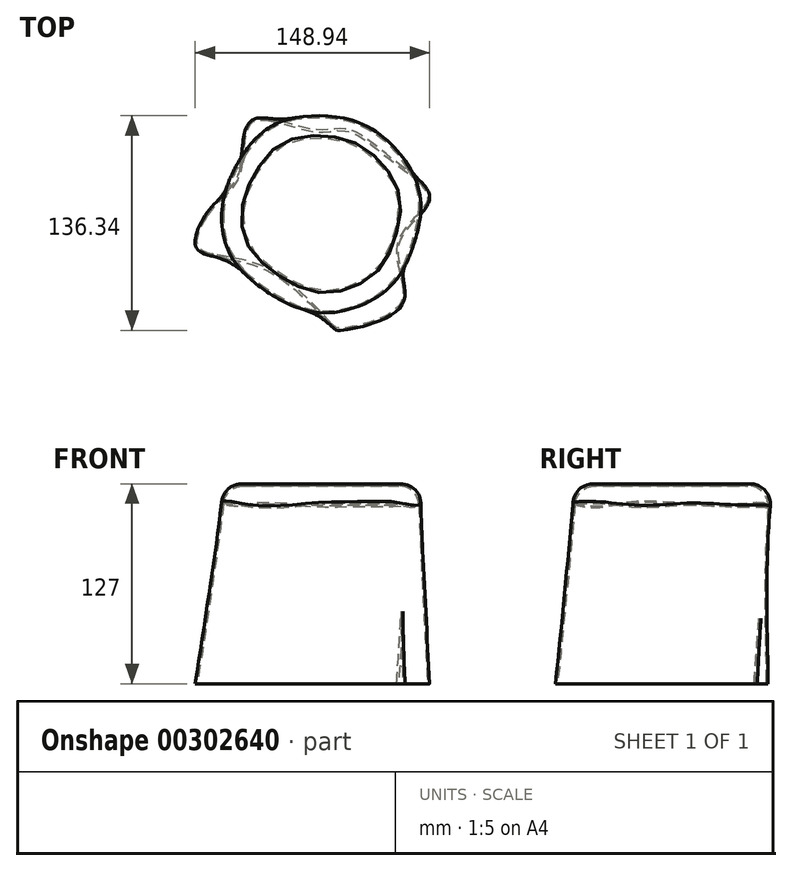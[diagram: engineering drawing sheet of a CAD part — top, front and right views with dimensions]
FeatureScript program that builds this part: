
annotation { "Feature Type Name" : "Feature", "Feature Type Description" : "" }
export const myFeature = defineFeature(function(context is Context, id is Id, definition is map)
    precondition{}
    {
        {
            var Q0;
            Q0=qCreatedBy(makeId("Top.planeOp"),FACE);
            cPlane(context, id + "F0", {"entities" : qUnion([Q0]), "cplaneType" : CPlaneType.OFFSET, "offset" : 127 * mm, "width" : 152.4 * mm, "height" : 152.4 * mm});
        }
        {
            var Q0;
            Q0=qCreatedBy(id+"F0.planeOp",FACE);
            var sketch = newSketch(context, id + "F1", { "sketchPlane" : qUnion([Q0])});
            skCircle(sketch, "E0", {"center": v(0, 0) * mm, "radius": 62.58 * mm});
            skSolve(sketch);
        }
        {
            var Q0;
            Q0=qCreatedBy(makeId("Top.planeOp"),FACE);
            var sketch = newSketch(context, id + "F2", { "sketchPlane" : qUnion([Q0])});
            skFitSpline(sketch, "E1", {"points": [v(-6.24, 52.9) * mm, v(-44.65, 58.66) * mm, v(-53.1, 25.24) * mm, v(-70, 3.72) * mm, v(-79.61, -22.4) * mm, v(-38.5, -35.08) * mm, v(6.06, -72.34) * mm, v(12.59, -74.65) * mm, v(51, -58.13) * mm, v(49.08, -20.1) * mm, v(68.3, 8.72) * mm, v(45.24, 33.7) * mm, v(16.81, 52.9) * mm, v(-6.24, 52.9) * mm]});
            skSolve(sketch);
        }
        {
            var Q0;
            Q0=makeQuery(id+"F1.imprint","IMPRINT",FACE,{"disambiguationData":[TD([[makeQuery(id+"F1.imprint","IMPRINT",EDGE,{"derivedFrom":sQuery(id+"F1.wireOp",EDGE,"E0")}),1.0]])]});
            var Q1;
            Q1=makeQuery(id+"F2.imprint","IMPRINT",FACE,{"disambiguationData":[TD([[makeQuery(id+"F2.imprint","IMPRINT",EDGE,{"derivedFrom":sQuery(id+"F2.wireOp",EDGE,"E1")}),1.0]])]});
            loft(context, id + "F3", {"sheetProfilesArray" : [{ "sheetProfileEntities" : qUnion([Q0]) }, { "sheetProfileEntities" : qUnion([Q1]) }]});
        }
        {
            var Q0;
            Q0=makeQuery(id+"F3.opLoft","CAP_FACE",FACE,{"disambiguationData":[OSD([makeQuery(id+"F2.imprint","IMPRINT",FACE,{"disambiguationData":[TD([[makeQuery(id+"F2.imprint","IMPRINT",EDGE,{"derivedFrom":sQuery(id+"F2.wireOp",EDGE,"E1")}),1.0]])]})])],"isStart":true});
            shell(context, id + "F4", {"entities" : qUnion([Q0]), "thickness" : 1.27 * mm});
        }
        {
            var Q0;
            Q0=makeQuery(id+"F4.opShell","OFFSET_EDGE",EDGE,{"disambiguationData":[OSD([sQuery(id+"F1.wireOp",EDGE,"E0")])]});
            var Q1;
            Q1=makeQuery(id+"F3.opLoft","MID_CAP_EDGE",EDGE,{"disambiguationData":[OSD([sQuery(id+"F1.wireOp",EDGE,"E0")])],"capPos":0.0});
            fillet(context, id + "F5", {"entities" : qUnion([Q0, Q1]), "radius" : 12.7 * mm, "tangentPropagation" : true, "allowEdgeOverflow" : false});
        }
    });
